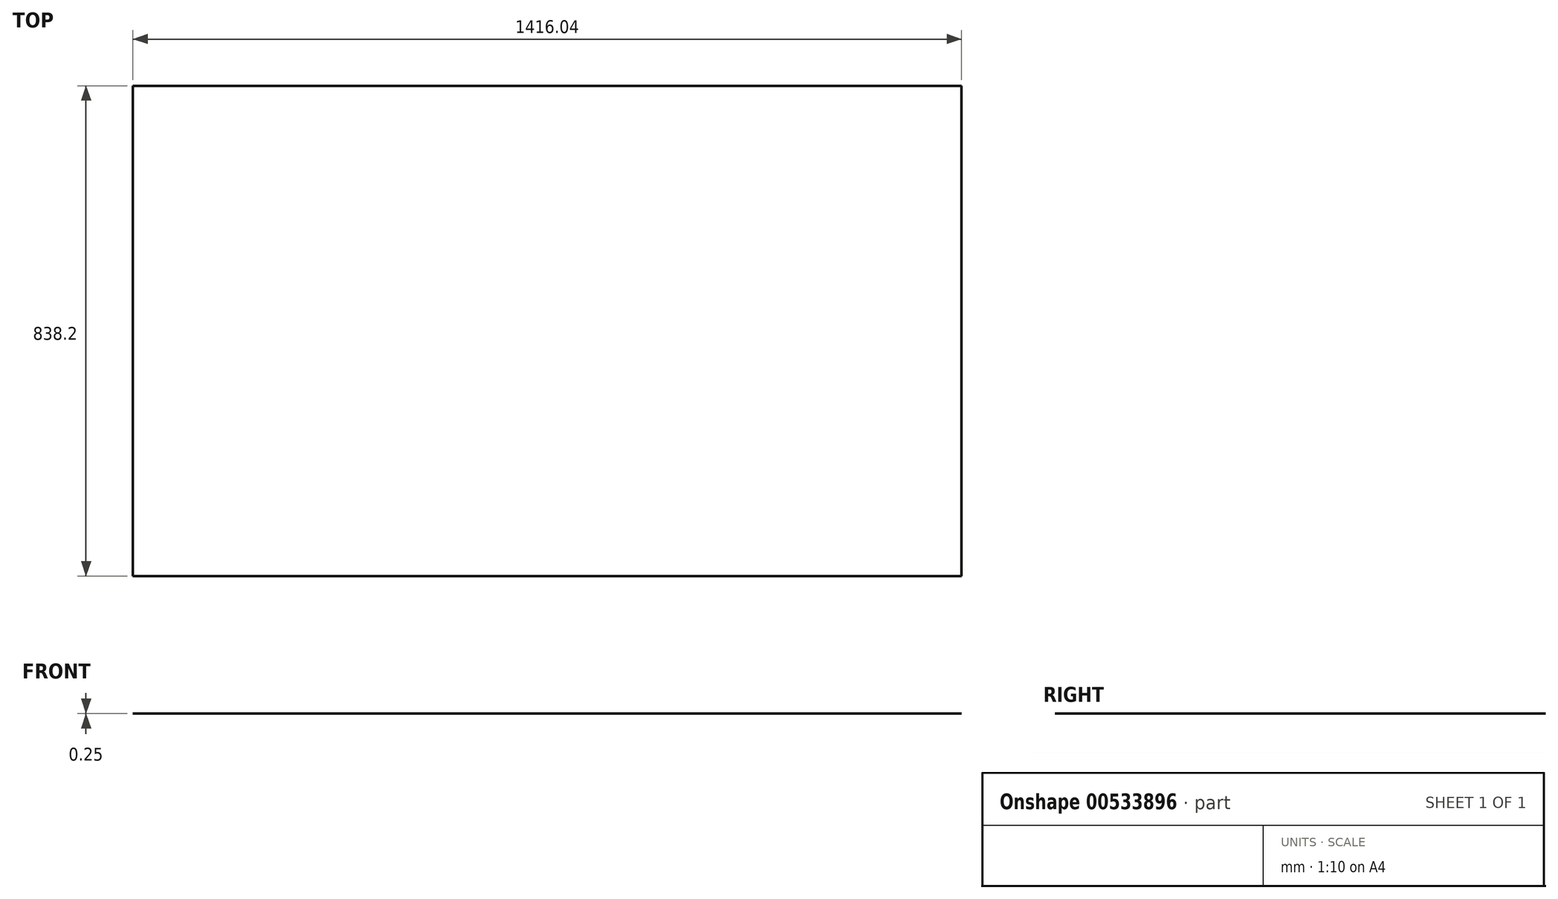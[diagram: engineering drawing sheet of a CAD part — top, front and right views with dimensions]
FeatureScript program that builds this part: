
annotation { "Feature Type Name" : "Feature", "Feature Type Description" : "" }
export const myFeature = defineFeature(function(context is Context, id is Id, definition is map)
    precondition{}
    {
        {
            var Q0;
            Q0=qCreatedBy(makeId("Top.planeOp"),FACE);
            var sketch = newSketch(context, id + "F0", { "sketchPlane" : qUnion([Q0])});
            skLineSegment(sketch, "E0.bottom", {"start": v(-708.02, -419.1) * mm, "end": v(708.03, -419.1) * mm});
            skLineSegment(sketch, "E0.top", {"start": v(-708.03, 419.1) * mm, "end": v(708.02, 419.1) * mm});
            skLineSegment(sketch, "E0.left", {"start": v(-708.02, -419.1) * mm, "end": v(-708.03, 419.1) * mm});
            skLineSegment(sketch, "E0.right", {"start": v(708.03, -419.1) * mm, "end": v(708.02, 419.1) * mm});
            skPoint(sketch, "E0.middle", {"position": v(0, 0) * mm});
            skSolve(sketch);
        }
        {
            var Q0;
            Q0 = qSketchRegion(id + "F0", true);
            extrude(context, id + "F1", {"entities" : qUnion([Q0]), "depth" : 0.25 * mm, "offsetDistance" : 25.4 * mm});
        }
    });
